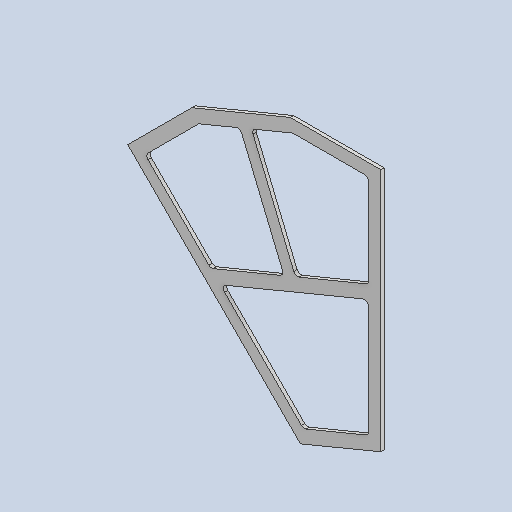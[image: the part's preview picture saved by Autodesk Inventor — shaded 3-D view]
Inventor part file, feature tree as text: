
AUTODESK INVENTOR PART (.ipt)
format: ipt  version: 2025 (Build 290162010, 162A)  size: 163,328 bytes
history: native  units: mm
features: other x3, sketch x2
ambient origin geometry x8: Origin, YZ Plane, XZ Plane, XY Plane, X Axis, Y Axis, Z Axis, Center Point
bodies: Solid1 (feature_tree)
feature tree (5):
  other  "ДМС 201 Внешняя рамка"
  other  "Solid1::ДМС 201 Внешняя рамка"
  other  "TaggingFeature1"
  sketch  "Sketch1"  dims[d0=10.0mm]
  sketch  "Sketch2"
